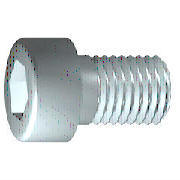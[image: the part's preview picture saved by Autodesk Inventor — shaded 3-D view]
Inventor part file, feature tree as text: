
AUTODESK INVENTOR PART (.ipt)
format: ipt  version: 2013 (Build 170138000, 138)  size: 190,976 bytes
history: native  units: mm (DEFAULTED — no unit token found)
features: sketch x2, extrude x1, plane x1, fillet x1
ambient origin geometry x7: Origin, YZ Plane, XY Plane, X Axis, Y Axis, Z Axis, Center Point
bodies: Solid1 (feature_tree), Body (feature_tree)
feature tree (5):
  extrude  "Slot"  Depth=0.306825mm
  plane  "Work Plane1"
  fillet  "Fillet2"  Radius=3.0mm
  sketch  "Sketch1"  dims[d1=8.693275mm d2=0.306825mm d3=3.0mm]
  sketch  "Sketch2"  dims[d4=1.5mm d5=60.0deg d6=3.0mm d7=3.0mm d8=2.886751mm d9=5.5mm d10=90.0deg d11=10.0mm d12=0.0mm d13=8.693275mm d14=0.0mm d15=0.306725mm d16=0.306725mm d17=0.3mm d19=0.0mm d26=10.0mm d27=45.0deg d28=0.0mm d29=0.0mm d30=0.1mm]
